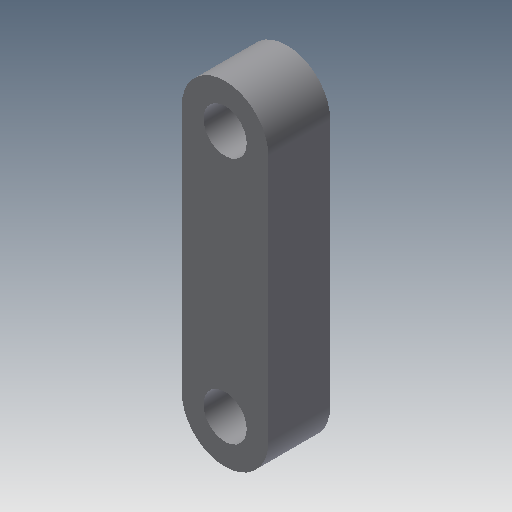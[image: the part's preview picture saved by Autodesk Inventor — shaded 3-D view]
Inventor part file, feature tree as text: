
AUTODESK INVENTOR PART (.ipt)
format: ipt  version: 2018 (Build 220112000, 112)  size: 104,448 bytes
history: native  units: mm
features: extrude x2, sketch x2
ambient origin geometry x8: Origin, YZ Plane, XZ Plane, XY Plane, X Axis, Y Axis, Z Axis, Center Point
bodies: Solid1 (feature_tree)
feature tree (4):
  extrude  "Extrusion1"  Depth=20.0mm
  extrude  "Extrusion2"  Depth=5.0mm TaperAngle=0.0deg
  sketch  "Sketch1"  dims[d0=7.0mm d1=20.0mm]
  sketch  "Sketch2"  dims[d2=7.0mm d3=5.0mm d4=0.0mm d5=3.5mm d6=3.5mm d7=5.0mm d8=0.0mm]
